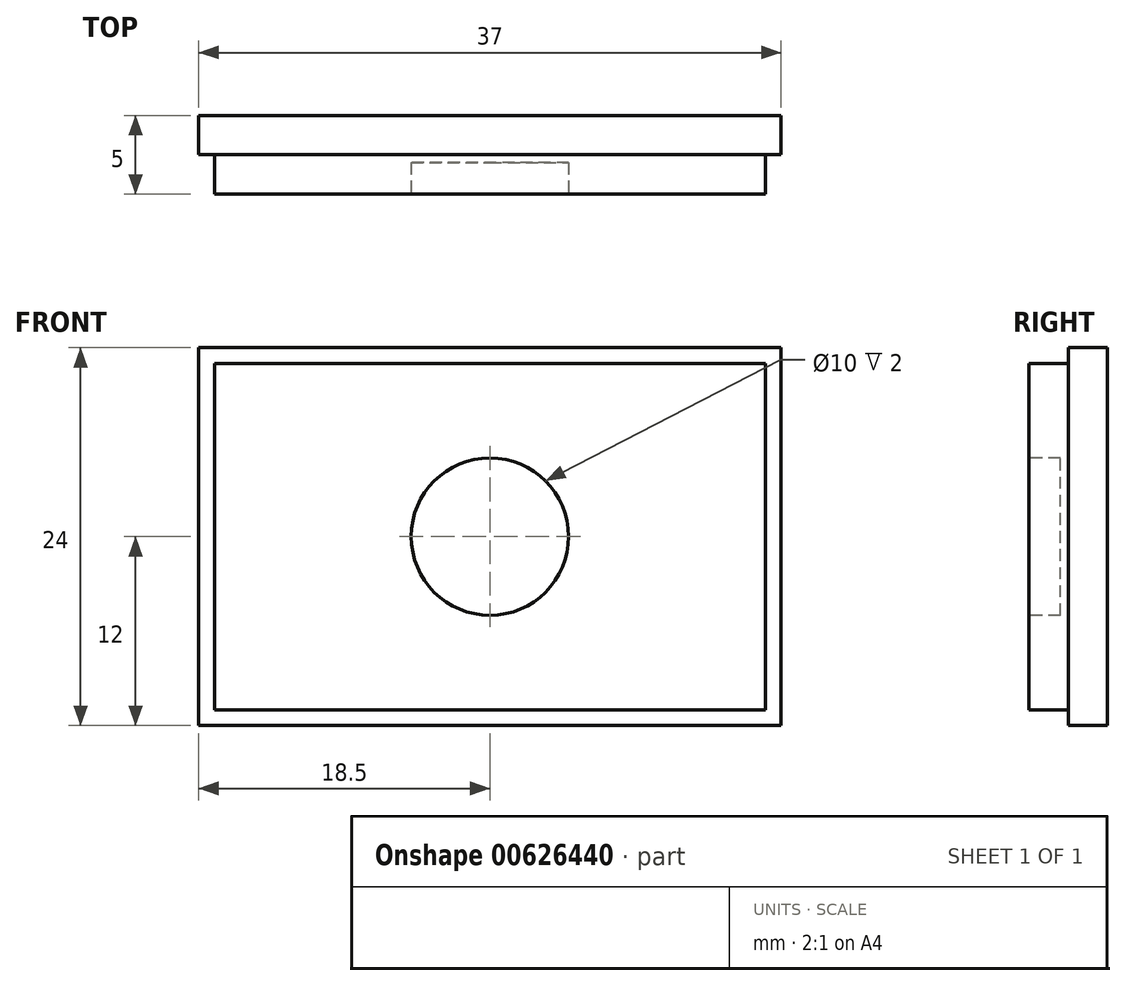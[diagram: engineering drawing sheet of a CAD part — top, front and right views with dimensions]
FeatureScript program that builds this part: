
annotation { "Feature Type Name" : "Feature", "Feature Type Description" : "" }
export const myFeature = defineFeature(function(context is Context, id is Id, definition is map)
    precondition{}
    {
        {
            var Q0;
            Q0=qCreatedBy(makeId("Front.planeOp"),FACE);
            var sketch = newSketch(context, id + "F0", { "sketchPlane" : qUnion([Q0])});
            skLineSegment(sketch, "E0.bottom", {"start": v(-18.5, 12) * mm, "end": v(18.5, 12) * mm});
            skLineSegment(sketch, "E0.top", {"start": v(-18.5, -12) * mm, "end": v(18.5, -12) * mm});
            skLineSegment(sketch, "E0.left", {"start": v(-18.5, 12) * mm, "end": v(-18.5, -12) * mm});
            skLineSegment(sketch, "E0.right", {"start": v(18.5, 12) * mm, "end": v(18.5, -12) * mm});
            skPoint(sketch, "E0.middle", {"position": v(0, 0) * mm});
            skSolve(sketch);
        }
        {
            var Q0;
            Q0=makeQuery(id+"F0.imprint","IMPRINT",FACE,{"disambiguationData":[TD([[makeQuery(id+"F0.imprint","IMPRINT",EDGE,{"derivedFrom":sQuery(id+"F0.wireOp",EDGE,"E0.bottom")}),-1.0]])]});
            extrude(context, id + "F1", {"entities" : qUnion([Q0]), "depth" : 2.5 * mm, "offsetDistance" : 25 * mm});
        }
        {
            var Q0;
            Q0=makeQuery(id+"F1.opExtrude","CAP_FACE",FACE,{"disambiguationData":[OSD([sQuery(id+"F0.wireOp",EDGE,"E0.bottom"),sQuery(id+"F0.wireOp",EDGE,"E0.top"),sQuery(id+"F0.wireOp",EDGE,"E0.left"),sQuery(id+"F0.wireOp",EDGE,"E0.right")])],"isStart":false});
            var sketch = newSketch(context, id + "F2", { "sketchPlane" : qUnion([Q0])});
            skLineSegment(sketch, "E1.0", {"start": v(-17.5, 11) * mm, "end": v(-17.5, -11) * mm});
            skLineSegment(sketch, "E1.1", {"start": v(17.5, 11) * mm, "end": v(-17.5, 11) * mm});
            skLineSegment(sketch, "E1.2", {"start": v(17.5, -11) * mm, "end": v(17.5, 11) * mm});
            skLineSegment(sketch, "E1.3", {"start": v(-17.5, -11) * mm, "end": v(17.5, -11) * mm});
            skSolve(sketch);
        }
        {
            var Q0;
            Q0=makeQuery(id+"F2.imprint","IMPRINT",FACE,{"disambiguationData":[TD([[makeQuery(id+"F2.imprint","IMPRINT",EDGE,{"derivedFrom":sQuery(id+"F2.wireOp",EDGE,"E1.0")}),1.0]])]});
            extrude(context, id + "F3", {"entities" : qUnion([Q0]), "operationType" : NewBodyOperationType.ADD, "depth" : 2.5 * mm, "offsetDistance" : 25 * mm});
        }
        {
            var Q0;
            Q0=makeQuery(id+"F3.opExtrude","CAP_FACE",FACE,{"disambiguationData":[OSD([sQuery(id+"F2.wireOp",EDGE,"E1.0"),sQuery(id+"F2.wireOp",EDGE,"E1.1"),sQuery(id+"F2.wireOp",EDGE,"E1.2"),sQuery(id+"F2.wireOp",EDGE,"E1.3")])],"isStart":false});
            var sketch = newSketch(context, id + "F4", { "sketchPlane" : qUnion([Q0])});
            skCircle(sketch, "E2", {"center": v(0, 0) * mm, "radius": 5 * mm});
            skSolve(sketch);
        }
        {
            var Q0;
            Q0 = qSketchRegion(id + "F4", true);
            extrude(context, id + "F5", {"entities" : qUnion([Q0]), "operationType" : NewBodyOperationType.REMOVE, "oppositeDirection" : true, "depth" : 2 * mm, "offsetDistance" : 25 * mm});
        }
    });
